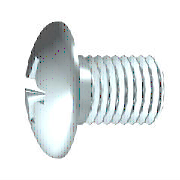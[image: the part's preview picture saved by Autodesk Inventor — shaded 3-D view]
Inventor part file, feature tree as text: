
AUTODESK INVENTOR PART (.ipt)
format: ipt  version: 2015 (Build 190159000, 159)  size: 264,192 bytes
history: native  units: mm (DEFAULTED — no unit token found)
features: sketch x1, plane x1, extrude x1, other x1
ambient origin geometry x7: Origin, YZ Plane, XZ Plane, X Axis, Y Axis, Z Axis, Center Point
bodies: Solid1 (feature_tree), Body (feature_tree)
feature tree (4):
  sketch  "Sketch1"  dims[d1=3.0mm d2=1.96mm d15=90.0deg d3=-2.4mm d4=45.0deg d5=0.966667mm d6=2.9mm d7=0.37mm d8=24.0mm d9=0.0mm d12=10.821041mm d13=4.625123mm d16=2.9mm d17=1.45mm d52=10.0mm d18=0.872665mm d54=90.0deg d19=0.148mm d20=0.0mm d21=3.0mm d22=24.0mm d23=0.306725mm d24=2.4mm d25=5.0mm d27=1.0mm d29=5.6mm d30=25.0mm d72=0.0mm d73=0.0mm d74=0.1mm]
  plane  "Workplane"
  extrude  "Slot"  Depth=0.1mm
  other  "Cut"
